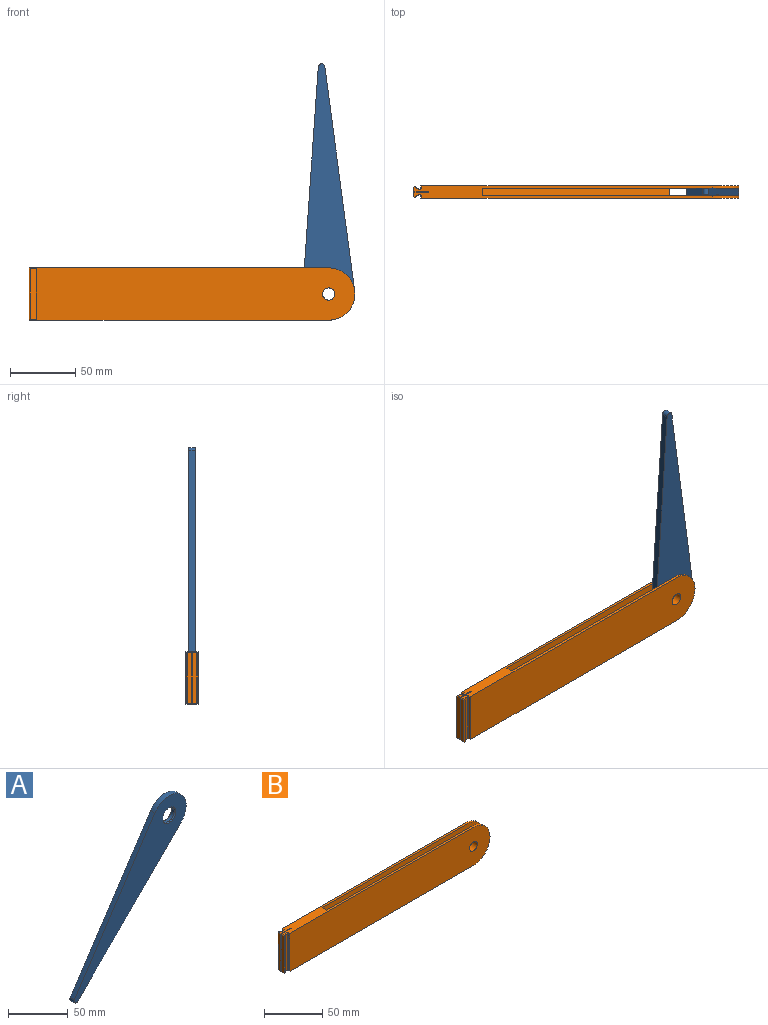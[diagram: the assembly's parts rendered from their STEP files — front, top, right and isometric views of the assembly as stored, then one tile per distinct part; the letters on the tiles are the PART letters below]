
ASSEMBLY  parts=2 mates=1
PART A: 9 faces, bbox 132.2x5x157 mm
  f0: cylinder r=20mm len=36.69mm, axis (0,-1,0), area 334.4mm2, adj f1,f4,f5,f6
  f1: plane 144.12x95.13mm, normal (-0.83,0,0.55), area 863.4mm2, adj f0,f2,f5,f6
  f2: cylinder r=2.5mm len=5mm, axis (0,-1,0), area 36.7mm2, adj f1,f4,f5,f6
  f3: cylinder r=6.87mm len=13.73mm, axis (0,-1,0), area 129.4mm2, adj f7,f8
  f4: plane 122.11x122.11mm, normal (0.71,0,-0.71), area 863.4mm2, adj f0,f2,f5,f6
  f5: plane 156.98x132.23mm, normal (0,1,0), area 4368.9mm2, adj f0,f1,f2,f4,f8
  f6: plane 156.98x132.23mm, normal (0,-1,0), area 4368.9mm2, adj f0,f1,f2,f4,f7
  f7: cone r=6.87mm half-angle=45deg, axis (0,-1,0), area 65.5mm2, adj f3,f6
  f8: cone r=7.87mm half-angle=45deg, axis (0,1,0), area 65.5mm2, adj f3,f5
PART B: 48 faces, bbox 249x9.4x40 mm
  f0: plane 38.76x3.4mm, normal (-1,0,0), area 131.8mm2, adj f22,f24,f28,f29
  f1: plane 228.38x9.4mm, normal (0,0,1), area 1161.7mm2, adj f3,f6,f8,f10,f11,f12,f13,f21
  f2: plane 38.76x2mm, normal (-1,0,0), area 77.5mm2, adj f11,f41,f45,f47
  f3: plane 196.27x40mm, normal (0,1,0), area 4571mm2, adj f1,f5,f6,f13,f14,f15,f16
  f4: plane 38.76x2mm, normal (-1,0,0), area 77.5mm2, adj f8,f26,f32,f35
  f5: plane 228.38x9.4mm, normal (0,0,-1), area 1912.9mm2, adj f3,f6,f8,f10,f11,f12,f14,f21
  f6: cylinder r=20mm len=40mm, axis (0,-1,0), area 125.7mm2, adj f1,f3,f5,f8
  f7: cylinder r=4.67mm len=9.4mm, axis (0,-1,0), area 275.6mm2, adj f8,f11
  f8: plane 243x40mm, normal (0,-1,0), area 9479.5mm2, adj f1,f4,f5,f6,f7,f26,f35
  f9: cylinder r=6.67mm len=13.33mm, axis (0,-1,0), area 142.4mm2, adj f16,f17
  f10: cylinder r=20mm len=40mm, axis (0,1,0), area 125.7mm2, adj f1,f5,f11,f12
  f11: plane 243x40mm, normal (0,1,0), area 9479.5mm2, adj f1,f2,f5,f7,f10,f41,f47
  f12: plane 196.27x40mm, normal (0,-1,0), area 4571mm2, adj f1,f5,f10,f13,f14,f15,f17
  f13: plane 5.4x5.2mm, normal (1,0,0), area 28.1mm2, adj f1,f3,f12,f15
  f14: plane 6.21x5.4mm, normal (0.83,0,-0.55), area 40.2mm2, adj f3,f5,f12,f15
  f15: plane 143.2x28.59mm, normal (0.2,0,0.98), area 788.6mm2, adj f3,f12,f13,f14
  f16: cone r=7.67mm half-angle=45deg, axis (0,-1,0), area 63.7mm2, adj f3,f9
  f17: cone r=7.67mm half-angle=45deg, axis (0,1,0), area 63.7mm2, adj f9,f12
  f18: plane 38.76x4.21mm, normal (0.45,0.89,0), area 182.5mm2, adj f39,f40,f44,f45
  f19: plane 38.76x4.21mm, normal (0.45,-0.89,0), area 182.5mm2, adj f27,f28,f32,f33
  f20: plane 38.76x3.4mm, normal (-1,0,0), area 131.8mm2, adj f21,f36,f38,f39
  f21: plane 40x11.7mm, normal (0,-1,0), area 467.6mm2, adj f1,f5,f20,f23,f36,f38
  f22: plane 40x11.7mm, normal (0,1,0), area 467.6mm2, adj f0,f1,f5,f23,f24,f29
  f23: cylinder r=0.3mm len=40mm, axis (0,0,1), area 37.7mm2, adj f1,f5,f21,f22
  f24: plane 3.4x0.62mm, normal (-0.71,0,-0.71), area 3mm2, adj f0,f5,f22,f25
  f25: plane 0.89x0.62mm, normal (-0.47,-0.75,-0.47), area 0.4mm2, adj f24,f27,f28
  f26: plane 2x0.62mm, normal (-0.71,0,-0.71), area 1.7mm2, adj f4,f5,f8,f30
  f27: plane 4.49x2.66mm, normal (0.32,-0.63,-0.71), area 4.1mm2, adj f5,f19,f25,f30
  f28: plane 38.76x0.89mm, normal (-0.53,-0.85,0), area 40.8mm2, adj f0,f19,f25,f31
  f29: plane 3.4x0.62mm, normal (-0.71,0,0.71), area 3mm2, adj f0,f1,f22,f31
  f30: plane 1.79x1.11mm, normal (-0.47,-0.75,-0.47), area 1.1mm2, adj f5,f26,f27,f32
  f31: plane 0.89x0.62mm, normal (-0.47,-0.75,0.47), area 0.4mm2, adj f28,f29,f33
  f32: plane 38.76x0.89mm, normal (-0.53,-0.85,0), area 40.8mm2, adj f4,f19,f30,f34
  f33: plane 4.49x2.66mm, normal (0.32,-0.63,0.71), area 4.1mm2, adj f1,f19,f31,f34
  f34: plane 1.79x1.11mm, normal (-0.47,-0.75,0.47), area 1.1mm2, adj f1,f32,f33,f35
  f35: plane 2x0.62mm, normal (-0.71,0,0.71), area 1.7mm2, adj f1,f4,f8,f34
  f36: plane 3.4x0.62mm, normal (-0.71,0,-0.71), area 3mm2, adj f5,f20,f21,f37
  f37: plane 0.89x0.62mm, normal (-0.47,0.75,-0.47), area 0.4mm2, adj f36,f39,f40
  f38: plane 3.4x0.62mm, normal (-0.71,0,0.71), area 3mm2, adj f1,f20,f21,f42
  f39: plane 38.76x0.89mm, normal (-0.53,0.85,0), area 40.8mm2, adj f18,f20,f37,f42
  f40: plane 4.49x2.66mm, normal (0.32,0.63,-0.71), area 4.1mm2, adj f5,f18,f37,f43
  f41: plane 2x0.62mm, normal (-0.71,0,-0.71), area 1.7mm2, adj f2,f5,f11,f43
  f42: plane 0.89x0.62mm, normal (-0.47,0.75,0.47), area 0.4mm2, adj f38,f39,f44
  f43: plane 1.79x1.11mm, normal (-0.47,0.75,-0.47), area 1.1mm2, adj f5,f40,f41,f45
  f44: plane 4.49x2.66mm, normal (0.32,0.63,0.71), area 4.1mm2, adj f1,f18,f42,f46
  f45: plane 38.76x0.89mm, normal (-0.53,0.85,0), area 40.8mm2, adj f2,f18,f43,f46
  f46: plane 1.79x1.11mm, normal (-0.47,0.75,0.47), area 1.1mm2, adj f1,f44,f45,f47
  f47: plane 2x0.62mm, normal (-0.71,0,0.71), area 1.7mm2, adj f1,f2,f11,f46
PLACE A rot(axis=(0,1,0),139deg) t=(0,-2.7,0)mm
PLACE B t=(0,-2.7,0)mm
MATE revolute B.f7 <-> A.f3  axis (0,-1,0) through (0,0,0)mm
